# Revit family: WC-Close Coupled-Caroma Profile 4 Skew Trap Suite1
name_source: partatom
category: Plumbing Fixtures
revit_build: Autodesk Revit 2014 (Build: 20131024_2115(x64)
units: mm (PartAtom-declared; Revit-internal decimal feet)

## types (2) — shared parameters
Assembly Code = D2010110
CW Connection = Yes
CWFU = 2
Description = Caroma Profile 4 Skew Trap Close Coupled Suite
HW Connection = No
Hardware = Metal-Chrome-Caroma
Height_ANZRS = 818 mm
Keynote = WC
Length_ANZRS = 665 mm  [stored 2.18176 ft]
Manufacturer = GWA Bathrooms & Kitchens
Material_ANZRS = Porcelain-White-Caroma
Model = 977775SC
ModifiedIssue_ANZRS = 20140627.01 $
Type Comments = Vitreous China, White Only, LH or RH Skew Trap available, Hygienic snap-on detachable Seat
URL = http://www.caroma.com.au
Vent Connection = No
WELSRating_ANZRS = WELS 4 Star rated, 4.5/3L
WFU = 3
Waste Connection = Yes
Width_ANZRS = 406 mm  [stored 1.33202 ft]
zero-valued in all types: Default Elevation, WasteOutlet_ANZRS

## per-type parameters (varying)
| type | Connector Angle | Connector Offset | LH Skew | RH Skew |
| RH Skew | 0.00° | 140 mm  [stored 0.459318 ft] | No | Yes |
| LH Skew | 180.00° | -140 mm  [stored -0.459318 ft] | Yes | No |

note: [stored X ft] marks values corroborated as IEEE doubles in the binary element streams (Revit-internal decimal feet)

## geometry (parser evidence)
native form markers: Blend x8, Sweep x1
no freeform markers — native parametric forms only
